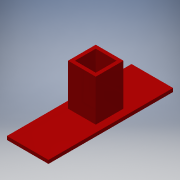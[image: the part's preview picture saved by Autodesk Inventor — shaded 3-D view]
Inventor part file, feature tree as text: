
AUTODESK INVENTOR PART (.ipt)
format: ipt  version: 2016 (Build 200138000, 138)  size: 114,688 bytes
history: native  units: in
note: dims shown in document units (in); Inventor stores cm internally (conversion verified against a paired STEP export)
features: extrude x3, sketch x2
ambient origin geometry x8: Origin, YZ Plane, XZ Plane, XY Plane, X Axis, Y Axis, Z Axis, Center Point
bodies: Solid1 (feature_tree)
feature tree (5):
  extrude  "Extrusion1"  Depth=4.5in
  sketch  "Sketch3"  dims[d2=0.125in d3=0.0in d8=1.0in d9=1.0in d10=0.25in d12=0.125in d13=1.5in d14=0.0in d15=0.2in d16=0.5in d17=0.5in d20=0.125in d21=0.0in d23=1.458in]
  extrude  "Extrusion3"  Depth=1.0in
  extrude  "Extrusion5"  Depth=1.0in
  sketch  "Sketch1"  dims[d0=1.5in d1=4.5in]
